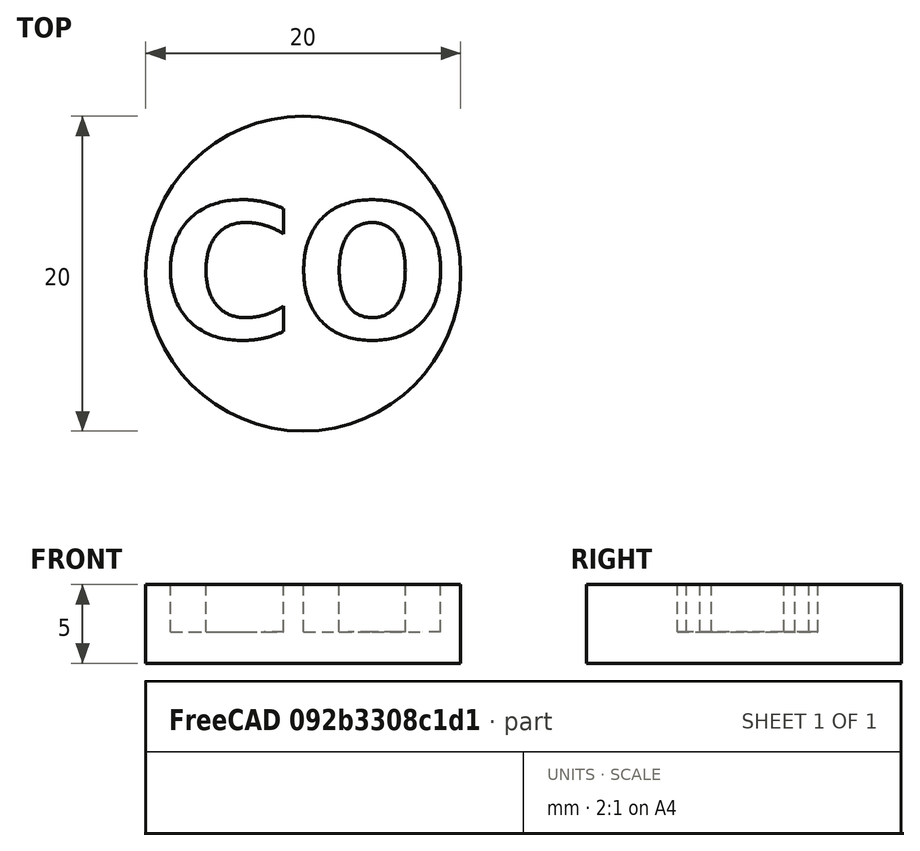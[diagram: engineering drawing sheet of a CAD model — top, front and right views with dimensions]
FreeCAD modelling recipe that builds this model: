
FCSTD DOCUMENT  (FreeCAD 0.20R27319 (Git))
Label: Stamp_C_O
License: All rights reserved
LicenseURL: http://en.wikipedia.org/wiki/All_rights_reserved
objects: Sketcher::SketchObject×1, PartDesign::Pad×1, PartDesign::Body×1, Part::Part2DObjectPython×1, Part::Extrusion×1, Part::Cut×1
note: 7 computed .brp shape members not serialized (recipe doc carries the construction recipe); baked Part::Feature solids carry a one-line shape summary decoded from their .brp

FEATURE [Sketcher::SketchObject] Sketch
  FullyConstrained = true
  MapMode = 5
  Support = -> [XY_Plane]
  sketch-geometry (1):
    g0: Circle CenterX=0 CenterY=0 CenterZ=0 NormalX=0 NormalY=0 NormalZ=1 AngleXU=0 Radius=10
  constraints (2):
    c: Coincident(g0,g-1)
    c: Diameter(g0) = 20
FEATURE [PartDesign::Pad] Pad
  Direction = (0,0,1)
  Length = 5
  Length2 = 10
  Profile = -> Sketch
  ReferenceAxis = -> Sketch [N_Axis]
  Type = 0
FEATURE [PartDesign::Body] Body
  Group = -> [Sketch,Pad]
  Origin = -> Origin
  Tip = -> Pad
FEATURE [Part::Part2DObjectPython] ShapeString  # Draft 2D object (typed FeaturePython)
  FontFile = <path>
  MakeFace = true
  Placement = pos=(-9,-3,-3) rot=(1,0,0;0rad)
  Size = 9
  String = CO
  Tracking = 0
FEATURE [Part::Extrusion] Extrude
  Base = -> ShapeString
  Dir = (0,0,1)
  DirMode = 2
  FaceMakerClass = Part::FaceMakerBullseye
  LengthFwd = 4
  LengthRev = 0
  Placement = pos=(0,-1,5) rot=(0,0,1;0rad)
  Solid = false
  Symmetric = false
FEATURE [Part::Cut] Cut
  Base = -> Pad
  Tool = -> Extrude
note: 1 file-system path scrubbed to <path> (originals preserved in the JSON sidecar)
